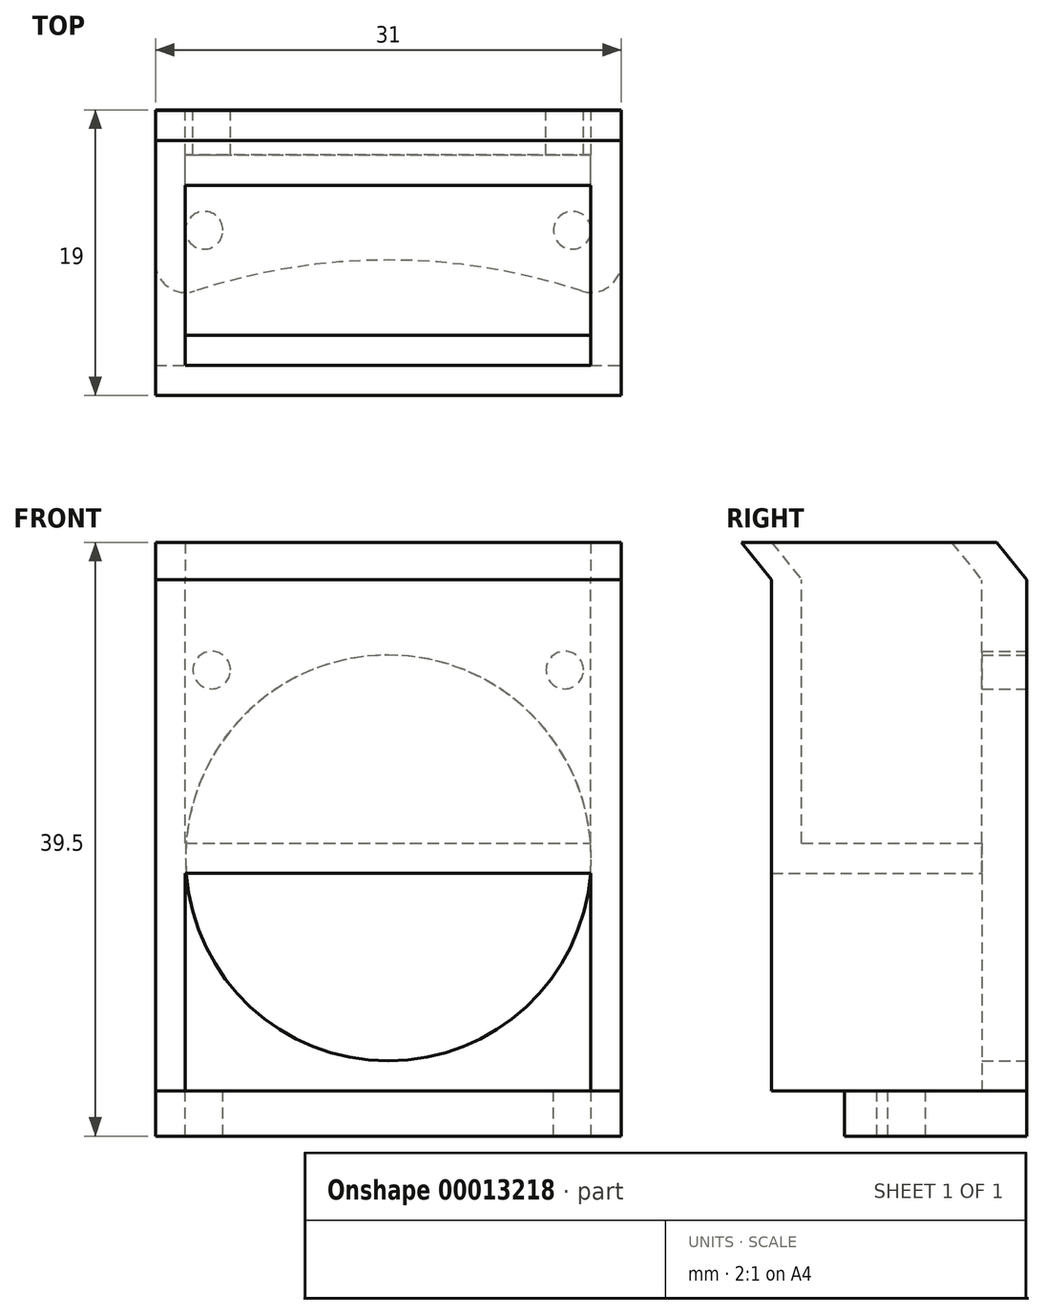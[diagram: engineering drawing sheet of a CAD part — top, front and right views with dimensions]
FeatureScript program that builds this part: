
annotation { "Feature Type Name" : "Feature", "Feature Type Description" : "" }
export const myFeature = defineFeature(function(context is Context, id is Id, definition is map)
    precondition{}
    {
        {
            var Q0;
            Q0=qCreatedBy(makeId("Top.planeOp"),FACE);
            var sketch = newSketch(context, id + "F0", { "sketchPlane" : qUnion([Q0])});
            skLineSegment(sketch, "E0.bottom", {"start": v(-20.87, 16.27) * mm, "end": v(10.13, 16.27) * mm});
            skLineSegment(sketch, "E0.left", {"start": v(-20.87, 16.27) * mm, "end": v(-20.87, 6.27) * mm});
            skLineSegment(sketch, "E0.right", {"start": v(10.13, 16.27) * mm, "end": v(10.13, 6.27) * mm});
            skLineSegment(sketch, "E1.left", {"start": v(-20.87, 6.27) * mm, "end": v(-20.87, 3.27) * mm});
            skLineSegment(sketch, "E2.left", {"start": v(10.13, 6.27) * mm, "end": v(10.13, 3.27) * mm});
            skPoint(sketch, "E3", {"position": v(-17.62, 8.27) * mm});
            skPoint(sketch, "E4", {"position": v(6.88, 8.27) * mm});
            skArc(sketch, "E5", {"start": v(10.13, 3.27) * mm, "mid": v(-5.37, 6.29) * mm, "end": v(-20.87, 3.27) * mm});
            skSolve(sketch);
        }
        {
            var Q0;
            Q0 = qSketchRegion(id + "F0", true);
            extrude(context, id + "F1", {"entities" : qUnion([Q0]), "oppositeDirection" : true, "depth" : 3 * mm});
        }
        {
            var Q0;
            Q0=sQuery(id+"F0.wireOp",VERTEX,"E3");
            var Q1;
            Q1=sQuery(id+"F0.wireOp",VERTEX,"E4");
            var Q2;
            Q2=makeQuery(id+"F1.opExtrude","SWEPT_BODY",BODY,{"disambiguationData":[OSD([sQuery(id+"F0.wireOp",EDGE,"E0.bottom"),sQuery(id+"F0.wireOp",EDGE,"E0.left"),sQuery(id+"F0.wireOp",EDGE,"E0.right"),sQuery(id+"F0.wireOp",EDGE,"E1.left"),sQuery(id+"F0.wireOp",EDGE,"E2.left"),sQuery(id+"F0.wireOp",EDGE,"E5")])]});
            hole(context, id + "F2", {"style" : HoleStyle.SIMPLE, "holeDiameter" : 2.5 * mm, "endStyle" : HoleEndStyle.THROUGH, "locations" : qUnion([Q0, Q1]), "scope" : qUnion([Q2])});
        }
        {
            var Q0;
            Q0=makeQuery(id+"F1.opExtrude","SWEPT_EDGE",EDGE,{"disambiguationData":[OSD([sQuery(id+"F0.wireOp",EDGE,"E1.left"),sQuery(id+"F0.wireOp",EDGE,"E5")])]});
            var Q1;
            Q1=makeQuery(id+"F1.opExtrude","SWEPT_EDGE",EDGE,{"disambiguationData":[OSD([sQuery(id+"F0.wireOp",EDGE,"E2.left"),sQuery(id+"F0.wireOp",EDGE,"E5")])]});
            fillet(context, id + "F3", {"entities" : qUnion([Q0, Q1]), "radius" : 2 * mm, "tangentPropagation" : true, "allowEdgeOverflow" : false});
        }
        {
            var Q0;
            Q0=makeQuery(id+"F1.opExtrude","SWEPT_FACE",FACE,{"disambiguationData":[OSD([sQuery(id+"F0.wireOp",EDGE,"E0.bottom")])]});
            var sketch = newSketch(context, id + "F4", { "sketchPlane" : qUnion([Q0])});
            skLineSegment(sketch, "E6.bottom", {"start": v(-10.13, 0) * mm, "end": v(20.87, 0) * mm});
            skLineSegment(sketch, "E6.top", {"start": v(-10.13, 31) * mm, "end": v(20.87, 31) * mm});
            skLineSegment(sketch, "E6.left", {"start": v(-10.13, 0) * mm, "end": v(-10.13, 31) * mm});
            skLineSegment(sketch, "E6.right", {"start": v(20.87, 0) * mm, "end": v(20.87, 31) * mm});
            skPoint(sketch, "E7", {"position": v(-6.38, 28) * mm});
            skPoint(sketch, "E8", {"position": v(17.12, 28) * mm});
            skPoint(sketch, "E9", {"position": v(5.37, 15.5) * mm});
            skLineSegment(sketch, "E10.bottom", {"start": v(20.87, 31) * mm, "end": v(-10.13, 31) * mm});
            skLineSegment(sketch, "E10.top", {"start": v(20.87, 34) * mm, "end": v(-10.13, 34) * mm});
            skLineSegment(sketch, "E10.left", {"start": v(20.87, 31) * mm, "end": v(20.87, 34) * mm});
            skLineSegment(sketch, "E10.right", {"start": v(-10.13, 31) * mm, "end": v(-10.13, 34) * mm});
            skSolve(sketch);
        }
        {
            var Q0;
            Q0 = qSketchRegion(id + "F4", true);
            extrude(context, id + "F5", {"entities" : qUnion([Q0]), "oppositeDirection" : true, "depth" : 3 * mm});
        }
        {
            var Q0;
            Q0=sQuery(id+"F4.wireOp",VERTEX,"E9");
            var Q1;
            Q1=makeQuery(id+"F5.opExtrude","SWEPT_BODY",BODY,{"disambiguationData":[OSD([sQuery(id+"F4.wireOp",EDGE,"E6.bottom"),sQuery(id+"F4.wireOp",EDGE,"E6.top"),sQuery(id+"F4.wireOp",EDGE,"E6.left"),sQuery(id+"F4.wireOp",EDGE,"E6.right")])]});
            hole(context, id + "F6", {"style" : HoleStyle.SIMPLE, "holeDiameter" : 27 * mm, "endStyle" : HoleEndStyle.THROUGH, "locations" : qUnion([Q0]), "scope" : qUnion([Q1])});
        }
        {
            var Q0;
            Q0=sQuery(id+"F4.wireOp",VERTEX,"E8");
            var Q1;
            Q1=sQuery(id+"F4.wireOp",VERTEX,"E7");
            var Q2;
            Q2=makeQuery(id+"F5.opExtrude","SWEPT_BODY",BODY,{"disambiguationData":[OSD([sQuery(id+"F4.wireOp",EDGE,"E6.bottom"),sQuery(id+"F4.wireOp",EDGE,"E6.top"),sQuery(id+"F4.wireOp",EDGE,"E6.left"),sQuery(id+"F4.wireOp",EDGE,"E6.right")])]});
            hole(context, id + "F7", {"style" : HoleStyle.SIMPLE, "holeDiameter" : 2.5 * mm, "endStyle" : HoleEndStyle.THROUGH, "locations" : qUnion([Q0, Q1]), "scope" : qUnion([Q2])});
        }
        {
            var Q0;
            Q0=makeQuery(id+"F5.opExtrude","CAP_FACE",FACE,{"disambiguationData":[OSD([sQuery(id+"F4.wireOp",EDGE,"E6.bottom"),sQuery(id+"F4.wireOp",EDGE,"E6.top"),sQuery(id+"F4.wireOp",EDGE,"E6.left"),sQuery(id+"F4.wireOp",EDGE,"E6.right")])],"isStart":false});
            var sketch = newSketch(context, id + "F8", { "sketchPlane" : qUnion([Q0])});
            skLineSegment(sketch, "E11.bottom", {"start": v(-20.87, 0) * mm, "end": v(-18.87, 0) * mm});
            skLineSegment(sketch, "E11.top", {"start": v(-20.87, 14.5) * mm, "end": v(-18.87, 14.5) * mm});
            skLineSegment(sketch, "E11.left", {"start": v(-20.87, 0) * mm, "end": v(-20.87, 14.5) * mm});
            skLineSegment(sketch, "E11.right", {"start": v(-18.87, 0) * mm, "end": v(-18.87, 14.5) * mm});
            skLineSegment(sketch, "E12.bottom", {"start": v(10.13, 0) * mm, "end": v(8.13, 0) * mm});
            skLineSegment(sketch, "E12.top", {"start": v(10.13, 14.5) * mm, "end": v(8.13, 14.5) * mm});
            skLineSegment(sketch, "E12.left", {"start": v(10.13, 0) * mm, "end": v(10.13, 14.5) * mm});
            skLineSegment(sketch, "E12.right", {"start": v(8.13, 0) * mm, "end": v(8.13, 14.5) * mm});
            skLineSegment(sketch, "E13.bottom", {"start": v(-20.87, 14.5) * mm, "end": v(10.13, 14.5) * mm});
            skLineSegment(sketch, "E13.top", {"start": v(-20.87, 16.5) * mm, "end": v(10.13, 16.5) * mm});
            skLineSegment(sketch, "E13.left", {"start": v(-20.87, 14.5) * mm, "end": v(-20.87, 16.5) * mm});
            skLineSegment(sketch, "E13.right", {"start": v(10.13, 14.5) * mm, "end": v(10.13, 16.5) * mm});
            skLineSegment(sketch, "E14.top", {"start": v(-20.87, 16.5) * mm, "end": v(-18.87, 16.5) * mm});
            skLineSegment(sketch, "E14.left", {"start": v(-20.87, 16.5) * mm, "end": v(-20.87, 0) * mm});
            skLineSegment(sketch, "E14.right", {"start": v(-18.87, 16.5) * mm, "end": v(-18.87, 0) * mm});
            skLineSegment(sketch, "E15.bottom", {"start": v(10.13, 0) * mm, "end": v(8.09, 0) * mm});
            skLineSegment(sketch, "E15.top", {"start": v(10.13, 16.5) * mm, "end": v(8.09, 16.5) * mm});
            skLineSegment(sketch, "E15.left", {"start": v(10.13, 16.5) * mm, "end": v(10.13, 0) * mm});
            skLineSegment(sketch, "E15.right", {"start": v(8.09, 16.5) * mm, "end": v(8.09, 0) * mm});
            skLineSegment(sketch, "E16.bottom", {"start": v(-18.87, 16.5) * mm, "end": v(-20.87, 16.5) * mm});
            skLineSegment(sketch, "E16.top", {"start": v(-18.87, 34) * mm, "end": v(-20.87, 34) * mm});
            skLineSegment(sketch, "E16.left", {"start": v(-18.87, 16.5) * mm, "end": v(-18.87, 34) * mm});
            skLineSegment(sketch, "E16.right", {"start": v(-20.87, 16.5) * mm, "end": v(-20.87, 34) * mm});
            skLineSegment(sketch, "E17.top", {"start": v(10.13, 34) * mm, "end": v(8.09, 34) * mm});
            skLineSegment(sketch, "E17.left", {"start": v(10.13, 16.5) * mm, "end": v(10.13, 34) * mm});
            skLineSegment(sketch, "E17.right", {"start": v(8.09, 16.5) * mm, "end": v(8.09, 34) * mm});
            skLineSegment(sketch, "E18.top", {"start": v(10.13, 36.5) * mm, "end": v(8.09, 36.5) * mm});
            skLineSegment(sketch, "E18.left", {"start": v(10.13, 34) * mm, "end": v(10.13, 36.5) * mm});
            skLineSegment(sketch, "E18.right", {"start": v(8.09, 34) * mm, "end": v(8.09, 36.5) * mm});
            skLineSegment(sketch, "E19.bottom", {"start": v(-20.87, 34) * mm, "end": v(-18.87, 34) * mm});
            skLineSegment(sketch, "E19.top", {"start": v(-20.87, 36.5) * mm, "end": v(-18.87, 36.5) * mm});
            skLineSegment(sketch, "E19.left", {"start": v(-20.87, 34) * mm, "end": v(-20.87, 36.5) * mm});
            skLineSegment(sketch, "E19.right", {"start": v(-18.87, 34) * mm, "end": v(-18.87, 36.5) * mm});
            skSolve(sketch);
        }
        {
            var Q0;
            Q0 = qSketchRegion(id + "F8", true);
            extrude(context, id + "F9", {"entities" : qUnion([Q0]), "depth" : 14 * mm});
        }
        {
            var Q0;
            Q0=makeQuery(id+"F9.opExtrude","SWEPT_FACE",FACE,{"disambiguationData":[OSD([sQuery(id+"F8.wireOp",EDGE,"E15.left"),sQuery(id+"F8.wireOp",EDGE,"E17.left")])]});
            var sketch = newSketch(context, id + "F10", { "sketchPlane" : qUnion([Q0])});
            skLineSegment(sketch, "E20.bottom", {"start": v(-0.73, 34) * mm, "end": v(1.27, 34) * mm});
            skLineSegment(sketch, "E20.top", {"start": v(-0.73, 15.5) * mm, "end": v(1.27, 15.5) * mm});
            skLineSegment(sketch, "E20.left", {"start": v(-0.73, 34) * mm, "end": v(-0.73, 15.5) * mm});
            skLineSegment(sketch, "E20.right", {"start": v(1.27, 34) * mm, "end": v(1.27, 15.5) * mm});
            skLineSegment(sketch, "E21", {"start": v(16.27, 33.98) * mm, "end": v(13.27, 33.98) * mm});
            skLineSegment(sketch, "E22", {"start": v(1.27, 34) * mm, "end": v(-0.73, 36.5) * mm});
            skLineSegment(sketch, "E23", {"start": v(-0.73, 36.5) * mm, "end": v(-2.73, 36.5) * mm});
            skLineSegment(sketch, "E24", {"start": v(-2.73, 36.5) * mm, "end": v(-0.73, 34) * mm});
            skLineSegment(sketch, "E25", {"start": v(13.27, 33.98) * mm, "end": v(11.25, 36.5) * mm});
            skLineSegment(sketch, "E26", {"start": v(11.25, 36.5) * mm, "end": v(14.25, 36.5) * mm});
            skLineSegment(sketch, "E27", {"start": v(14.25, 36.5) * mm, "end": v(16.27, 33.98) * mm});
            skSolve(sketch);
        }
        {
            var Q0;
            Q0 = qSketchRegion(id + "F10", true);
            extrude(context, id + "F11", {"entities" : qUnion([Q0]), "operationType" : NewBodyOperationType.ADD, "oppositeDirection" : true, "depth" : 31 * mm});
        }
    });
